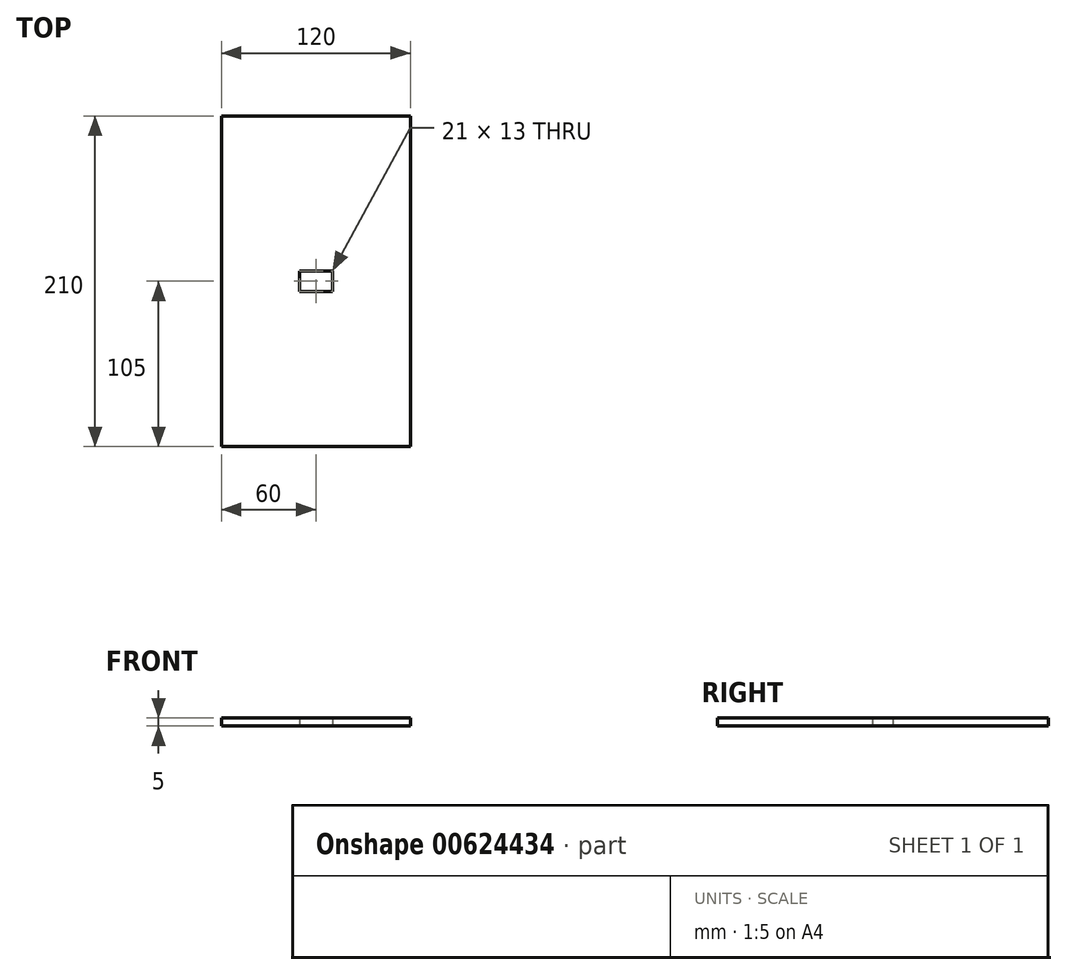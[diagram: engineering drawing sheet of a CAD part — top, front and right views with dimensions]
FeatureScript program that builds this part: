
annotation { "Feature Type Name" : "Feature", "Feature Type Description" : "" }
export const myFeature = defineFeature(function(context is Context, id is Id, definition is map)
    precondition{}
    {
        {
            var Q0;
            Q0=qCreatedBy(makeId("Top.planeOp"),FACE);
            var sketch = newSketch(context, id + "F0", { "sketchPlane" : qUnion([Q0])});
            skLineSegment(sketch, "E0.bottom", {"start": v(60, -105) * mm, "end": v(-60, -105) * mm});
            skLineSegment(sketch, "E0.top", {"start": v(60, 105) * mm, "end": v(-60, 105) * mm});
            skLineSegment(sketch, "E0.left", {"start": v(60, -105) * mm, "end": v(60, 105) * mm});
            skLineSegment(sketch, "E0.right", {"start": v(-60, -105) * mm, "end": v(-60, 105) * mm});
            skPoint(sketch, "E0.middle", {"position": v(0, 0) * mm});
            skLineSegment(sketch, "E1.bottom", {"start": v(10.5, 6.5) * mm, "end": v(-10.5, 6.5) * mm});
            skLineSegment(sketch, "E1.top", {"start": v(10.5, -6.5) * mm, "end": v(-10.5, -6.5) * mm});
            skLineSegment(sketch, "E1.left", {"start": v(10.5, 6.5) * mm, "end": v(10.5, -6.5) * mm});
            skLineSegment(sketch, "E1.right", {"start": v(-10.5, 6.5) * mm, "end": v(-10.5, -6.5) * mm});
            skSolve(sketch);
        }
        {
            var Q0;
            Q0 = qSketchRegion(id + "F0", true);
            extrude(context, id + "F1", {"entities" : qUnion([Q0]), "depth" : 5 * mm, "offsetDistance" : 25.4 * mm});
        }
    });
